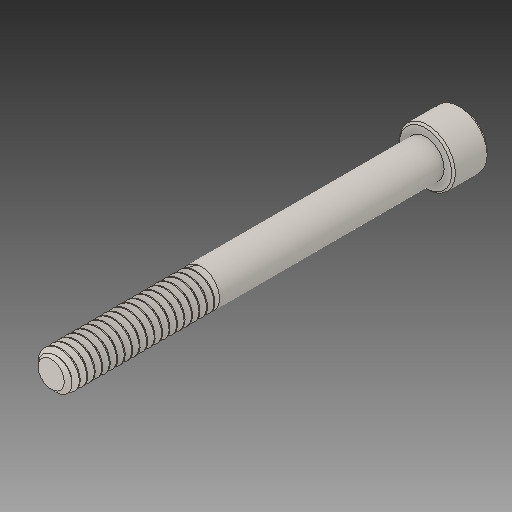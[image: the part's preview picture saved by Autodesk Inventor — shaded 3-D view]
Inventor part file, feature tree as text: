
AUTODESK INVENTOR PART (.ipt)
format: ipt  version: 2017 (Build 210142000, 142)  size: 648,192 bytes
history: native  units: in
note: dims shown in document units (in); Inventor stores cm internally (conversion verified against a paired STEP export)
features: chamfer x1
ambient origin geometry x8: Origin, YZ Plane, XZ Plane, XY Plane, X Axis, Y Axis, Z Axis, Center Point
bodies: Solid1 (feature_tree)
feature tree (1):
  chamfer  "Chamfer2"  [1 undecoded]
note: 1 required parameter value undecoded (feature->parameter linkage not recoverable at this tier; creation-order binding heuristic only, values carry confidence <= 0.55)
